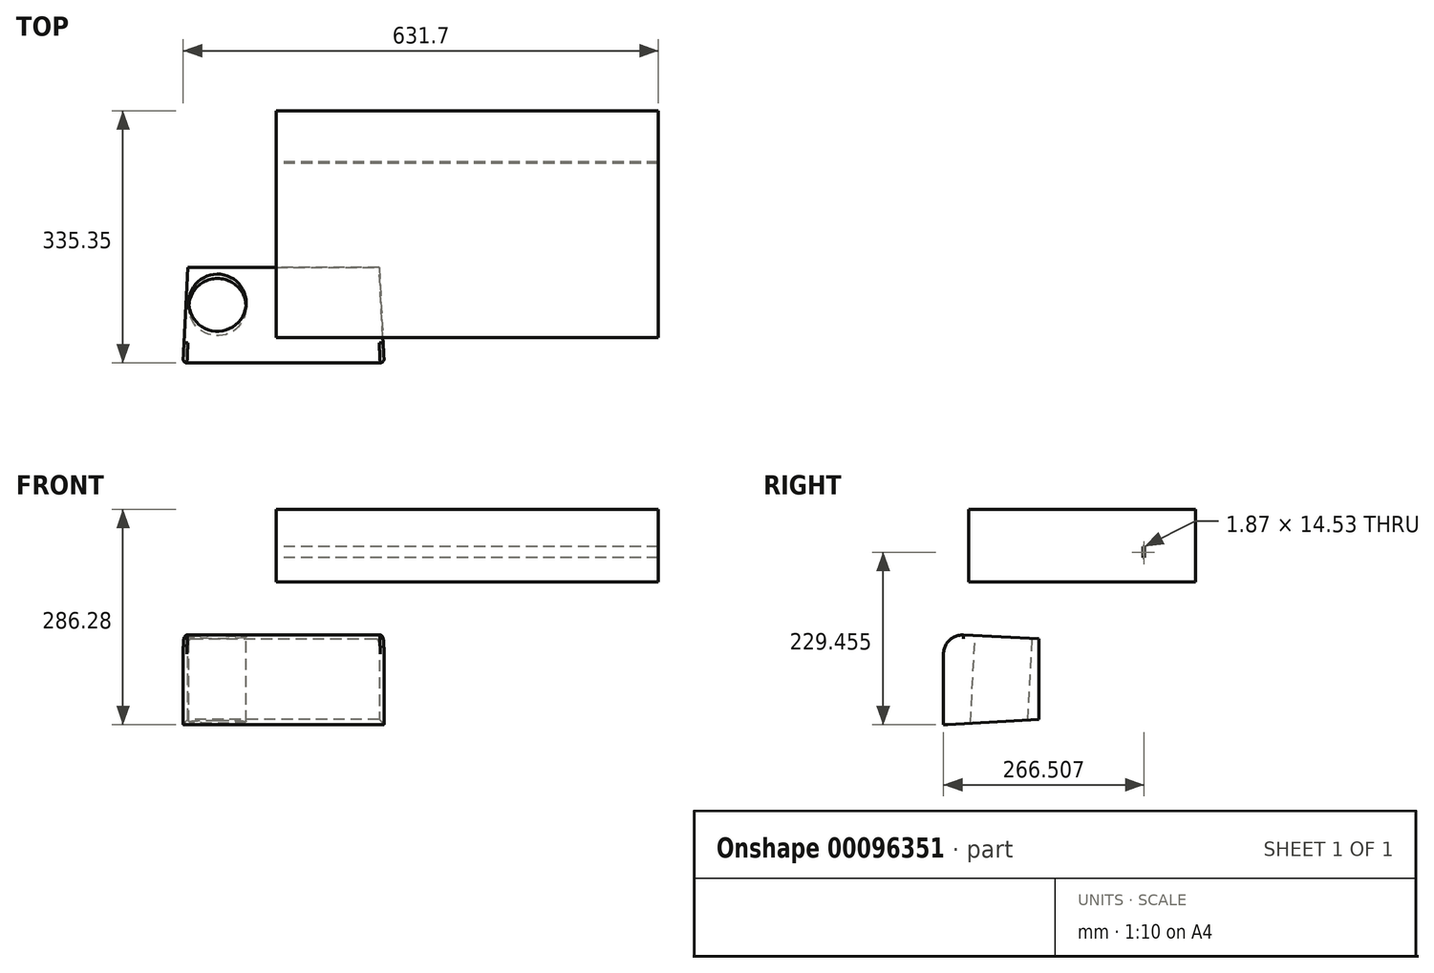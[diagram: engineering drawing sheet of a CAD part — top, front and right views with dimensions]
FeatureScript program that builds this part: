
annotation { "Feature Type Name" : "Feature", "Feature Type Description" : "" }
export const myFeature = defineFeature(function(context is Context, id is Id, definition is map)
    precondition{}
    {
        {
            var Q0;
            Q0=qCreatedBy(makeId("Front.planeOp"),FACE);
            var sketch = newSketch(context, id + "F0", { "sketchPlane" : qUnion([Q0])});
            skLineSegment(sketch, "E0.bottom", {"start": v(-117.32, 65.42) * mm, "end": v(136.87, 65.42) * mm});
            skLineSegment(sketch, "E0.top", {"start": v(-117.32, -41.9) * mm, "end": v(136.87, -41.9) * mm});
            skLineSegment(sketch, "E0.left", {"start": v(-117.32, 65.42) * mm, "end": v(-117.32, -41.9) * mm});
            skLineSegment(sketch, "E0.right", {"start": v(136.87, 65.42) * mm, "end": v(136.87, -41.9) * mm});
            skSolve(sketch);
        }
        {
            var Q0;
            Q0=makeQuery(id+"F0.imprint","IMPRINT",FACE,{"disambiguationData":[TD([[makeQuery(id+"F0.imprint","IMPRINT",EDGE,{"derivedFrom":sQuery(id+"F0.wireOp",EDGE,"E0.bottom")}),-1.0]])]});
            extrude(context, id + "F1", {"entities" : qUnion([Q0]), "depth" : 127 * mm, "hasDraft" : true, "draftAngle" : 3 * degree});
        }
        {
            var Q0;
            Q0=makeQuery(id+"F1.opExtrude","CAP_EDGE",EDGE,{"disambiguationData":[OSD([sQuery(id+"F0.wireOp",EDGE,"E0.bottom")])],"isStart":false});
            fillet(context, id + "F2", {"entities" : qUnion([Q0]), "radius" : 25.4 * mm, "tangentPropagation" : true, "allowEdgeOverflow" : false});
        }
        {
            var Q0;
            Q0=makeQuery(id+"F1.opExtrude","SWEPT_FACE",FACE,{"disambiguationData":[OSD([sQuery(id+"F0.wireOp",EDGE,"E0.bottom")])]});
            var sketch = newSketch(context, id + "F3", { "sketchPlane" : qUnion([Q0])});
            skPoint(sketch, "E1", {"position": v(-78.06, -50.47) * mm});
            skPoint(sketch, "E2", {"position": v(48.94, -50.46) * mm});
            skSolve(sketch);
        }
        {
            var Q0;
            Q0=sQuery(id+"F3.wireOp",VERTEX,"E1");
            var Q1;
            Q1=makeQuery(id+"F1.opExtrude","SWEPT_BODY",BODY,{"disambiguationData":[OSD([sQuery(id+"F0.wireOp",EDGE,"E0.bottom"),sQuery(id+"F0.wireOp",EDGE,"E0.top"),sQuery(id+"F0.wireOp",EDGE,"E0.left"),sQuery(id+"F0.wireOp",EDGE,"E0.right")])]});
            hole(context, id + "F4", {"style" : HoleStyle.SIMPLE, "endStyle" : HoleEndStyle.THROUGH, "holeDiameter" : 76.2 * mm, "locations" : qUnion([Q0]), "scope" : qUnion([Q1]), "isTappedThrough" : true});
        }
        {
            var Q0;
            Q0=makeQuery(id+"F1.opExtrude","SWEPT_EDGE",EDGE,{"disambiguationData":[OSD([sQuery(id+"F0.wireOp",EDGE,"E0.bottom"),sQuery(id+"F0.wireOp",EDGE,"E0.right")])]});
            fillet(context, id + "F5", {"entities" : qUnion([Q0]), "radius" : 5.08 * mm, "tangentPropagation" : true, "allowEdgeOverflow" : false});
        }
        {
            var Q0;
            Q0=makeQuery(id+"F2.opFillet","BLEND_EDGE",EDGE,{"blendedFrom":[makeQuery(id+"F1.opExtrude","CAP_EDGE",EDGE,{"disambiguationData":[OSD([sQuery(id+"F0.wireOp",EDGE,"E0.bottom")])],"isStart":false}),makeQuery(id+"F1.opExtrude","SWEPT_FACE",FACE,{"disambiguationData":[OSD([sQuery(id+"F0.wireOp",EDGE,"E0.left")])]})],"blendedInto":[makeQuery(id+"F1.opExtrude","SWEPT_FACE",FACE,{"disambiguationData":[OSD([sQuery(id+"F0.wireOp",EDGE,"E0.left")])]})]});
            fillet(context, id + "F6", {"entities" : qUnion([Q0]), "radius" : 5.08 * mm, "tangentPropagation" : true, "allowEdgeOverflow" : false});
        }
        {
            var Q0;
            Q0=qCreatedBy(makeId("Right.planeOp"),FACE);
            var sketch = newSketch(context, id + "F7", { "sketchPlane" : qUnion([Q0])});
            skLineSegment(sketch, "E3.bottom", {"start": v(138.57, 173.63) * mm, "end": v(140.44, 173.63) * mm});
            skLineSegment(sketch, "E3.top", {"start": v(138.57, 188.16) * mm, "end": v(140.44, 188.16) * mm});
            skLineSegment(sketch, "E3.left", {"start": v(138.57, 173.63) * mm, "end": v(138.57, 188.16) * mm});
            skLineSegment(sketch, "E3.right", {"start": v(140.44, 173.63) * mm, "end": v(140.44, 188.16) * mm});
            skLineSegment(sketch, "E4.bottom", {"start": v(208.35, 141.26) * mm, "end": v(-93.2, 141.26) * mm});
            skLineSegment(sketch, "E4.top", {"start": v(208.35, 237.72) * mm, "end": v(-93.2, 237.72) * mm});
            skLineSegment(sketch, "E4.left", {"start": v(208.35, 141.26) * mm, "end": v(208.35, 237.72) * mm});
            skLineSegment(sketch, "E4.right", {"start": v(-93.2, 141.26) * mm, "end": v(-93.2, 237.72) * mm});
            skSolve(sketch);
        }
        {
            var Q0;
            Q0=makeQuery(id+"F7.imprint","IMPRINT",FACE,{"disambiguationData":[TD([[makeQuery(id+"F7.imprint","IMPRINT",EDGE,{"derivedFrom":sQuery(id+"F7.wireOp",EDGE,"E3.bottom")}),-1.0]])]});
            extrude(context, id + "F8", {"entities" : qUnion([Q0]), "depth" : 508 * mm});
        }
    });
